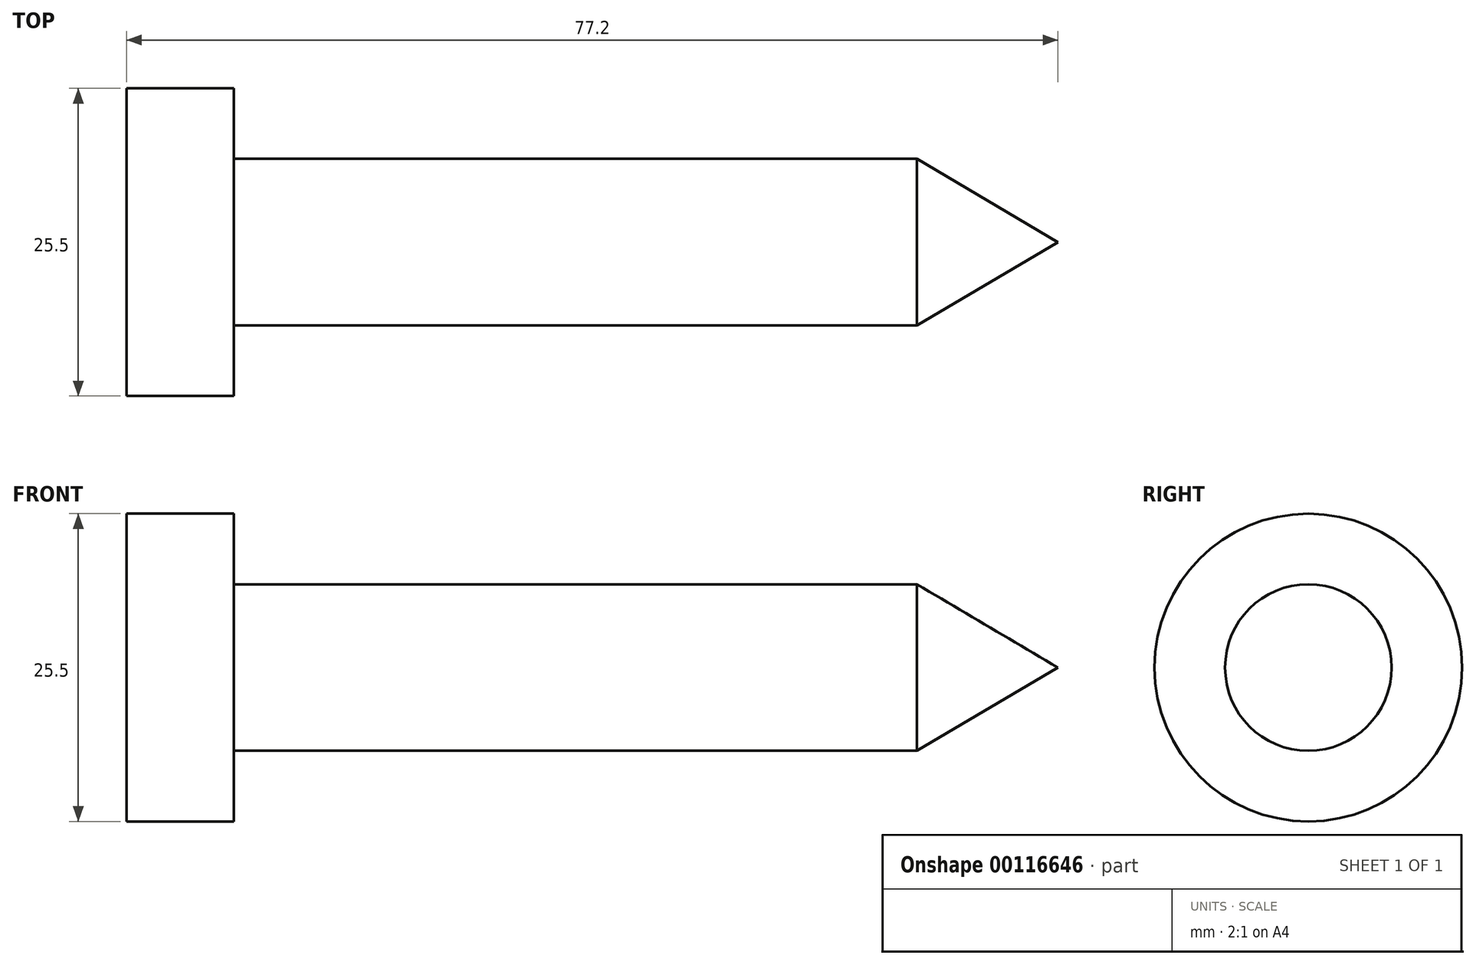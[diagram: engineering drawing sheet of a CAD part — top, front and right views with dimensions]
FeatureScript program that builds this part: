
annotation { "Feature Type Name" : "Feature", "Feature Type Description" : "" }
export const myFeature = defineFeature(function(context is Context, id is Id, definition is map)
    precondition{}
    {
        {
            var Q0;
            Q0=qCreatedBy(makeId("Front.planeOp"),FACE);
            var sketch = newSketch(context, id + "F0", { "sketchPlane" : qUnion([Q0])});
            skPoint(sketch, "E0.middle", {"position": v(0, 0) * mm});
            skLineSegment(sketch, "E1.bottom", {"start": v(-29, 0) * mm, "end": v(27.6, 0) * mm});
            skLineSegment(sketch, "E1.top", {"start": v(-29, 6.9) * mm, "end": v(27.6, 6.9) * mm});
            skLineSegment(sketch, "E1.left", {"start": v(-29, 0) * mm, "end": v(-29, 6.9) * mm});
            skLineSegment(sketch, "E1.right", {"start": v(27.6, 0) * mm, "end": v(27.6, 6.9) * mm});
            skLineSegment(sketch, "E2.bottom", {"start": v(-37.9, 12.75) * mm, "end": v(-29, 12.75) * mm});
            skLineSegment(sketch, "E2.top", {"start": v(-37.9, 0) * mm, "end": v(-29, 0) * mm});
            skLineSegment(sketch, "E2.left", {"start": v(-37.9, 12.75) * mm, "end": v(-37.9, 0) * mm});
            skLineSegment(sketch, "E2.right", {"start": v(-29, 12.75) * mm, "end": v(-29, 0) * mm});
            skLineSegment(sketch, "E3", {"start": v(27.6, 6.9) * mm, "end": v(39.3, 0) * mm});
            skLineSegment(sketch, "E4", {"start": v(27.6, 0) * mm, "end": v(39.3, 0) * mm});
            skSolve(sketch);
        }
        {
            var Q0;
            Q0=makeQuery(id+"F0.imprint","IMPRINT",FACE,{"disambiguationData":[TD([[makeQuery(id+"F0.imprint","IMPRINT",EDGE,{"derivedFrom":sQuery(id+"F0.wireOp",EDGE,"E1.right")}),-1.0]])]});
            var Q1;
            {var subQ2=sQuery(id+"F0.wireOp",EDGE,"E2.bottom");Q1=makeQuery(id+"F0.imprint","IMPRINT",FACE,{"disambiguationData":[TD([[makeQuery(id+"F0.imprint","IMPRINT",EDGE,{"derivedFrom":subQ2}),-1.0]])]});}
            var Q2;
            {var subQ0=sQuery(id+"F0.wireOp",EDGE,"E1.bottom");Q2=makeQuery(id+"F0.imprint","IMPRINT",FACE,{"disambiguationData":[TD([[makeQuery(id+"F0.imprint","IMPRINT",EDGE,{"derivedFrom":subQ0}),1.0]])]});}
            var Q3;
            Q3=sQuery(id+"F0.wireOp",EDGE,"E1.bottom");
            revolve(context, id + "F1", {"entities" : qUnion([Q0, Q1, Q2]), "axis" : qUnion([Q3]), "revolveType" : RevolveType.FULL});
        }
    });
